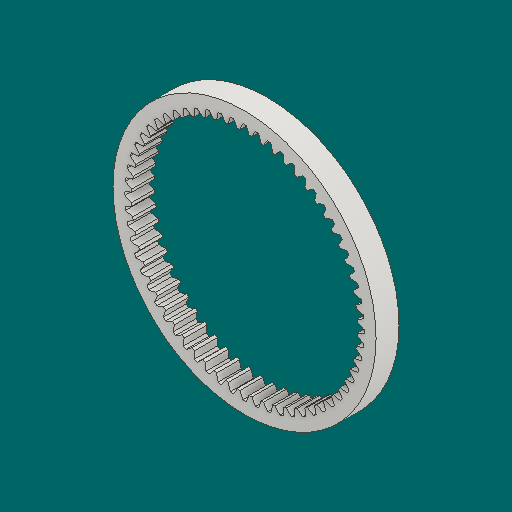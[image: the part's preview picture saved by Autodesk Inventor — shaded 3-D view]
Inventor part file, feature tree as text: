
AUTODESK INVENTOR PART (.ipt)
format: ipt  version: 2023.1 (Build 271208000, 208)  size: 373,760 bytes
history: native  units: mm (DEFAULTED — no unit token found)
features: plane x3, other x3, sketch x2, extrude x1
ambient origin geometry x8: Origin, YZ Plane, XZ Plane, XY Plane, X Axis, Y Axis, Z Axis, Center Point
bodies: Solid1 (feature_tree)
feature tree (9):
  extrude  "Extrusion1"  Depth=7.62mm TaperAngle=0.0deg
  plane  "Work Plane1"
  plane  "Work Plane2"
  plane  "Work Plane3"
  other  "Spur Gear"
  sketch  "Sketch1"  dims[d0=87.3125mm d1=7.62mm d2=0.0mm]
  sketch  "Sketch2"  dims[d3=76.2mm d4=76.2mm d5=0.0mm d6=0.0mm d7=0.523599mm d9=0.0mm d14=0.0mm d15=26.67mm d16=0.0mm d17=0.0mm d18=0.0mm d19=26.67mm]
  other  "Srf1"
  other  "Pitch Diameter"
